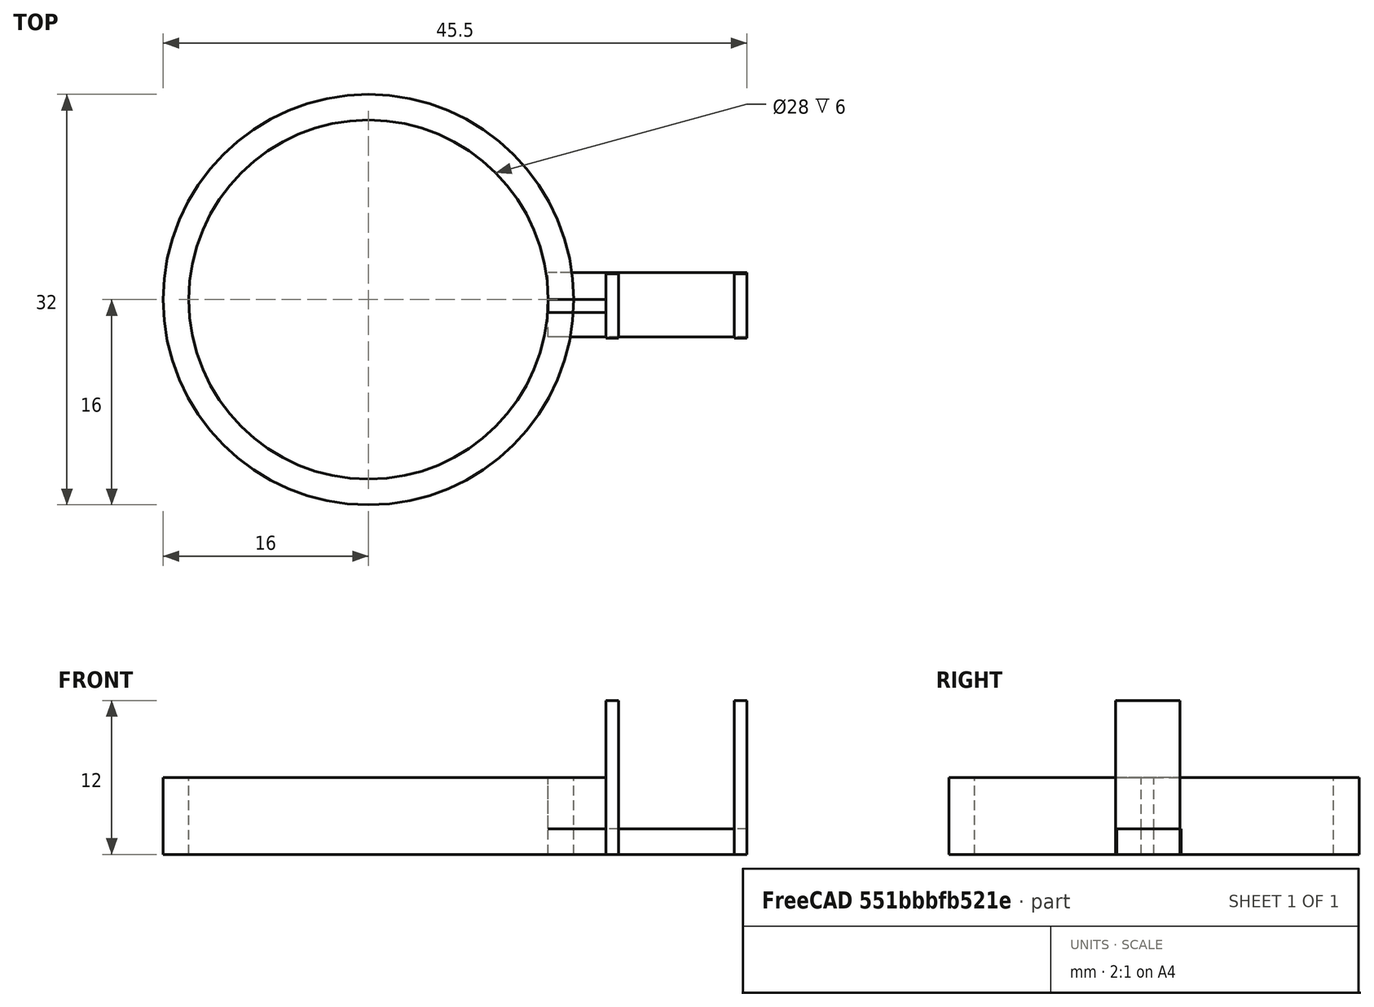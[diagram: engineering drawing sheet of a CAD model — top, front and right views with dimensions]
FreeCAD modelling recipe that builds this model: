
FCSTD DOCUMENT  (FreeCAD 0.18R16117 (Git))
Label: tf2
License: All rights reserved
LicenseURL: http://en.wikipedia.org/wiki/All_rights_reserved
objects: App::MeasureDistance×7, Part::Box×4, Part::Cylinder×2, Part::Cut×1, Part::FeaturePython×1, Part::Mirroring×1
note: 9 computed .brp shape members not serialized (recipe doc carries the construction recipe); baked Part::Feature solids carry a one-line shape summary decoded from their .brp

FEATURE [Part::Cylinder] Cylinder  label="Outer"
  Angle = 360
  AttacherType = Attacher::AttachEngine3D
  Height = 6
  Radius = 16
FEATURE [Part::Cylinder] Cylinder001  label="Inner"
  Angle = 360
  AttacherType = Attacher::AttachEngine3D
  Height = 6
  Radius = 14
FEATURE [Part::Cut] Cut  label="Ring"
  Base = -> Cylinder
  Tool = -> Cylinder001
FEATURE [Part::Box] Box002  label="Cube002"
  AttacherType = Attacher::AttachEngine3D
  Height = 12
  Length = 1
  Placement = pos=(-24,-3,0) rot=(0,0,1;0rad)
  Width = 5
FEATURE [Part::Box] Box003  label="Cube003"
  AttacherType = Attacher::AttachEngine3D
  Height = 6
  Length = 1
  Placement = pos=(-23,7e-15,0) rot=(0,0,-1;1.5708rad)
  Width = 4.5
FEATURE [Part::Box] Box  label="Cube"
  AttacherType = Attacher::AttachEngine3D
  Height = 2
  Length = 15.5
  Placement = pos=(-34,-2.9,0) rot=(0,0,1;0rad)
  Width = 5
FEATURE [Part::Box] Box001  label="Cube001"
  AttacherType = Attacher::AttachEngine3D
  Height = 12
  Length = 1
  Placement = pos=(-34,-3,0) rot=(0,0,1;0rad)
  Width = 5
FEATURE [App::MeasureDistance] Distance  label="Distance: 28.01 mm"
  Distance = 28.012
  P1 = (-14.0661,-1,6)
  P2 = (13.9458,-0.947253,6)
FEATURE [Part::FeaturePython] BooleanFragments  # WARN: FeaturePython — macro-defined, semantics opaque (R4)
  Mode = 0
  Objects = -> [Box003,Box001,Box002,Box]
  Placement = pos=(4.5,0,0) rot=(0,0,1;0rad)
  Tolerance = 0
FEATURE [Part::Mirroring] Part__Mirroring  label="BooleanFragments (Mirror #1)"
  Base = (0,0,0)
  Normal = (1,0,0)
  Source = -> BooleanFragments
FEATURE [App::MeasureDistance] Distance001  label="Distance: 39.00 mm"
  Distance = 39.0002
  P1 = (-19.5,-0.925723,10)
  P2 = (19.5,-1.06463,10)
FEATURE [App::MeasureDistance] Distance002  label="Distance: 57.04 mm"
  Distance = 57.0419
  P1 = (-28.5,0.856895,10)
  P2 = (28.5,-1.32842,10)
FEATURE [App::MeasureDistance] Distance003  label="Distance: 9.05 mm"
  Distance = 9.04741
  P1 = (-28.5,-3,6.55145)
  P2 = (-19.4766,-3,5.89244)
FEATURE [App::MeasureDistance] Distance004  label="Distance: 28.11 mm"
  Distance = 28.107
  P1 = (-14,-1,6)
  P2 = (14.107,-1,6)
FEATURE [App::MeasureDistance] Distance006  label="Distance: 5.00 mm"
  Distance = 5.00185
  P1 = (-29.1012,-3,10)
  P2 = (-28.9651,2,10)
FEATURE [App::MeasureDistance] Distance007  label="Distance: 11.85 mm"
  Distance = 11.8508
  P1 = (-29.5,-3,11.8691)
  P2 = (-29.5,-3,0.0182304)
